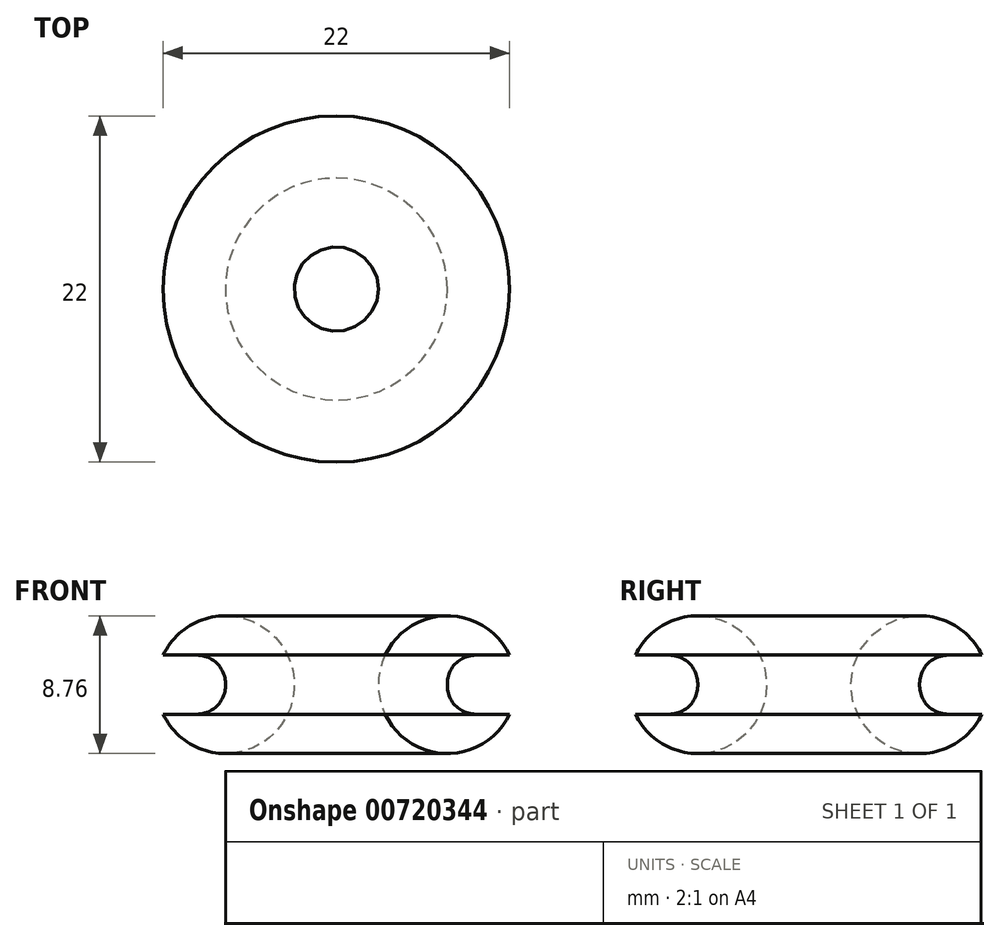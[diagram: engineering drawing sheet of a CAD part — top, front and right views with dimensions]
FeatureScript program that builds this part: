
annotation { "Feature Type Name" : "Feature", "Feature Type Description" : "" }
export const myFeature = defineFeature(function(context is Context, id is Id, definition is map)
    precondition{}
    {
        {
            var Q0;
            Q0=qCreatedBy(makeId("Front.planeOp"),FACE);
            var sketch = newSketch(context, id + "F0", { "sketchPlane" : qUnion([Q0])});
            skLineSegment(sketch, "E0", {"start": v(0, 6.53) * mm, "end": v(0, 4.38) * mm, "construction": true});
            skLineSegment(sketch, "E1.0", {"start": v(3.95, 1.87) * mm, "end": v(1.8, 1.87) * mm});
            skLineSegment(sketch, "E2.0", {"start": v(3.95, -1.88) * mm, "end": v(1.8, -1.88) * mm});
            skLineSegment(sketch, "E3", {"start": v(0, 0.07) * mm, "end": v(0, -0.08) * mm});
            skLineSegment(sketch, "E4", {"start": v(-3.95, 1.87) * mm, "end": v(-10.95, 1.87) * mm, "construction": true});
            skArc(sketch, "E5", {"start": v(3.95, 1.88) * mm, "mid": v(-4.38, 0) * mm, "end": v(3.95, -1.88) * mm});
            skLineSegment(sketch, "E6.trimOffspring", {"start": v(-4.38, 0) * mm, "end": v(-11.15, 0) * mm, "construction": true});
            skLineSegment(sketch, "E7.trimOffspring", {"start": v(-3.95, -1.88) * mm, "end": v(-10.82, -1.88) * mm, "construction": true});
            skLineSegment(sketch, "E8.0", {"start": v(-7.05, 1.87) * mm, "end": v(-7.05, -1.88) * mm, "construction": true});
            skPoint(sketch, "E9.orphan", {"position": v(-7.74, 1.87) * mm});
            skPoint(sketch, "E10.orphan", {"position": v(-7.74, -1.88) * mm});
            skPoint(sketch, "E11.orphan", {"position": v(-7.74, 0) * mm});
            skPoint(sketch, "E12.visualSharp", {"position": v(0, 1.87) * mm});
            skArc(sketch, "E12.filletArc", {"start": v(1.8, 1.87) * mm, "mid": v(0.53, 1.35) * mm, "end": v(0, 0.07) * mm});
            skPoint(sketch, "E13.visualSharp", {"position": v(0, -1.88) * mm});
            skArc(sketch, "E13.filletArc", {"start": v(0, -0.08) * mm, "mid": v(0.53, -1.35) * mm, "end": v(1.8, -1.88) * mm});
            skSolve(sketch);
        }
        {
            var Q0;
            Q0=makeQuery(id+"F0.imprint","IMPRINT",FACE,{"disambiguationData":[TD([[makeQuery(id+"F0.imprint","IMPRINT",EDGE,{"derivedFrom":sQuery(id+"F0.wireOp",EDGE,"E1.0")}),-1.0]])]});
            var Q1;
            Q1=sQuery(id+"F0.wireOp",EDGE,"E8.0");
            revolve(context, id + "F1", {"surfaceOperationType" : NewSurfaceOperationType.NEW, "entities" : qUnion([Q0]), "axis" : qUnion([Q1]), "revolveType" : RevolveType.FULL});
        }
    });
